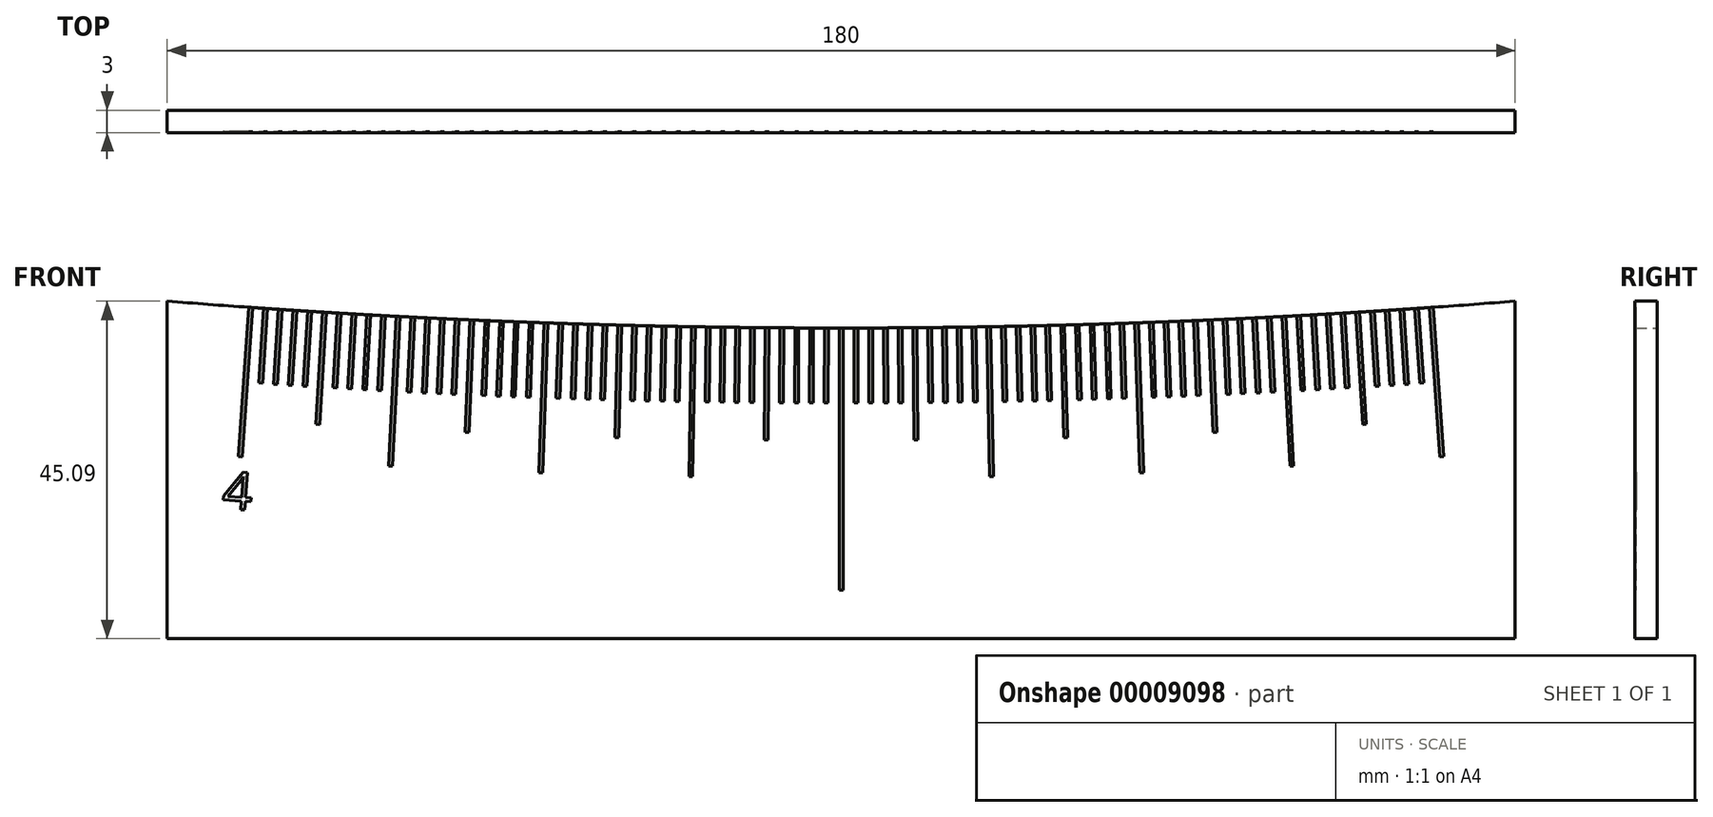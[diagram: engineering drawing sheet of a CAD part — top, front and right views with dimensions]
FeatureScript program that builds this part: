
annotation { "Feature Type Name" : "Feature", "Feature Type Description" : "" }
export const myFeature = defineFeature(function(context is Context, id is Id, definition is map)
    precondition{}
    {
        {
            var Q0;
            Q0=qCreatedBy(makeId("Front.planeOp"),FACE);
            var sketch = newSketch(context, id + "F0", { "sketchPlane" : qUnion([Q0])});
            skCircle(sketch, "E0", {"center": v(0, 1130) * mm, "radius": 1130 * mm});
            skLineSegment(sketch, "E1.rect.bottom", {"start": v(90, -41.5) * mm, "end": v(-90, -41.5) * mm});
            skLineSegment(sketch, "E1.rect.top", {"start": v(90, 41.5) * mm, "end": v(-90, 41.5) * mm});
            skLineSegment(sketch, "E1.rect.left", {"start": v(90, -41.5) * mm, "end": v(90, 41.5) * mm});
            skLineSegment(sketch, "E1.rect.right", {"start": v(-90, -41.5) * mm, "end": v(-90, 41.5) * mm});
            skPoint(sketch, "E1.rect.middle", {"position": v(0, 0) * mm});
            skSolve(sketch);
        }
        {
            var Q0;
            {var subQ3=sQuery(id+"F0.wireOp",EDGE,"E1.rect.bottom");Q0=makeQuery(id+"F0.imprint","IMPRINT",FACE,{"disambiguationData":[TD([[makeQuery(id+"F0.imprint","IMPRINT",EDGE,{"derivedFrom":subQ3}),-1.0]])]});}
            extrude(context, id + "F1", {"entities" : qUnion([Q0]), "depth" : 3 * mm});
        }
        {
            var Q0;
            Q0=makeQuery(id+"F1.opExtrude","CAP_FACE",FACE,{"disambiguationData":[OSD([sQuery(id+"F0.wireOp",EDGE,"E0"),sQuery(id+"F0.wireOp",EDGE,"E1.rect.bottom"),sQuery(id+"F0.wireOp",EDGE,"E1.rect.left"),sQuery(id+"F0.wireOp",EDGE,"E1.rect.right")])],"isStart":false});
            var sketch = newSketch(context, id + "F2", { "sketchPlane" : qUnion([Q0])});
            skLineSegment(sketch, "E2.rect.bottom", {"start": v(0.25, 20) * mm, "end": v(-0.25, 20) * mm});
            skLineSegment(sketch, "E2.rect.top", {"start": v(0.25, -20) * mm, "end": v(-0.25, -20) * mm});
            skLineSegment(sketch, "E2.rect.left", {"start": v(0.25, 20) * mm, "end": v(0.25, -20) * mm});
            skLineSegment(sketch, "E2.rect.right", {"start": v(-0.25, 20) * mm, "end": v(-0.25, -20) * mm});
            skPoint(sketch, "E2.rect.middle", {"position": v(0, 0) * mm});
            skLineSegment(sketch, "E3.1.0", {"start": v(-19.12, 20.16) * mm, "end": v(-19.62, 20.17) * mm});
            skLineSegment(sketch, "E3.1.1", {"start": v(-19.62, 20.17) * mm, "end": v(-20.32, -19.82) * mm});
            skLineSegment(sketch, "E3.1.2", {"start": v(-19.12, 20.16) * mm, "end": v(-19.82, -19.83) * mm});
            skLineSegment(sketch, "E3.1.3", {"start": v(-19.82, -19.83) * mm, "end": v(-20.32, -19.82) * mm});
            skLineSegment(sketch, "E3.2.0", {"start": v(-38.49, 20.67) * mm, "end": v(-38.99, 20.68) * mm});
            skLineSegment(sketch, "E3.2.1", {"start": v(-38.99, 20.68) * mm, "end": v(-40.38, -19.3) * mm});
            skLineSegment(sketch, "E3.2.2", {"start": v(-38.49, 20.67) * mm, "end": v(-39.88, -19.3) * mm});
            skLineSegment(sketch, "E3.2.3", {"start": v(-39.88, -19.3) * mm, "end": v(-40.38, -19.3) * mm});
            skLineSegment(sketch, "E3.3.0", {"start": v(-57.84, 21.5) * mm, "end": v(-58.34, 21.53) * mm});
            skLineSegment(sketch, "E3.3.1", {"start": v(-58.34, 21.53) * mm, "end": v(-60.44, -18.41) * mm});
            skLineSegment(sketch, "E3.3.2", {"start": v(-57.84, 21.5) * mm, "end": v(-59.94, -18.44) * mm});
            skLineSegment(sketch, "E3.3.3", {"start": v(-59.94, -18.44) * mm, "end": v(-60.44, -18.41) * mm});
            skLineSegment(sketch, "E3.4.0", {"start": v(-77.18, 22.69) * mm, "end": v(-77.68, 22.72) * mm});
            skLineSegment(sketch, "E3.4.1", {"start": v(-77.68, 22.72) * mm, "end": v(-80.47, -17.18) * mm});
            skLineSegment(sketch, "E3.4.2", {"start": v(-77.18, 22.69) * mm, "end": v(-79.97, -17.22) * mm});
            skLineSegment(sketch, "E3.4.3", {"start": v(-79.97, -17.22) * mm, "end": v(-80.47, -17.18) * mm});
            skPoint(sketch, "E3.center", {"position": v(0, 1130) * mm});
            skLineSegment(sketch, "E3.anchor1", {"start": v(0, 1130) * mm, "end": v(-0.25, 20) * mm, "construction": true});
            skLineSegment(sketch, "E3.anchor2", {"start": v(0, 1130) * mm, "end": v(-77.68, 22.72) * mm, "construction": true});
            skSolve(sketch);
        }
        {
            var Q0;
            Q0 = qSketchRegion(id + "F2", true);
            extrude(context, id + "F3", {"entities" : qUnion([Q0]), "operationType" : NewBodyOperationType.REMOVE, "oppositeDirection" : true, "depth" : 0.1 * mm});
        }
        {
            var Q0;
            Q0=makeQuery(id+"F1.opExtrude","SWEPT_BODY",BODY,{"disambiguationData":[OSD([sQuery(id+"F0.wireOp",EDGE,"E0"),sQuery(id+"F0.wireOp",EDGE,"E1.rect.bottom"),sQuery(id+"F0.wireOp",EDGE,"E1.rect.left"),sQuery(id+"F0.wireOp",EDGE,"E1.rect.right")])]});
            var Q1;
            Q1=qCreatedBy(makeId("Right.planeOp"),FACE);
            mirror(context, id + "F4", {"operationType" : NewBodyOperationType.INTERSECT, "entities" : qUnion([Q0]), "mirrorPlane" : qUnion([Q1])});
        }
        {
            var Q0;
            Q0=makeQuery(id+"F1.opExtrude","CAP_FACE",FACE,{"disambiguationData":[OSD([sQuery(id+"F0.wireOp",EDGE,"E0"),sQuery(id+"F0.wireOp",EDGE,"E1.rect.bottom"),sQuery(id+"F0.wireOp",EDGE,"E1.rect.left"),sQuery(id+"F0.wireOp",EDGE,"E1.rect.right")])],"isStart":false});
            var sketch = newSketch(context, id + "F5", { "sketchPlane" : qUnion([Q0])});
            skLineSegment(sketch, "E4.rect.bottom", {"start": v(0.25, 10) * mm, "end": v(-0.25, 10) * mm});
            skLineSegment(sketch, "E4.rect.top", {"start": v(0.25, -10) * mm, "end": v(-0.25, -10) * mm});
            skLineSegment(sketch, "E4.rect.left", {"start": v(0.25, 10) * mm, "end": v(0.25, -10) * mm});
            skLineSegment(sketch, "E4.rect.right", {"start": v(-0.25, 10) * mm, "end": v(-0.25, -10) * mm});
            skPoint(sketch, "E4.rect.middle", {"position": v(0, 0) * mm});
            skLineSegment(sketch, "E5.1.0", {"start": v(-1.74, -10) * mm, "end": v(-2.24, -10) * mm});
            skLineSegment(sketch, "E5.1.1", {"start": v(-1.7, 10) * mm, "end": v(-1.74, -10) * mm});
            skLineSegment(sketch, "E5.1.2", {"start": v(-2.2, 10) * mm, "end": v(-2.24, -10) * mm});
            skLineSegment(sketch, "E5.1.3", {"start": v(-1.7, 10) * mm, "end": v(-2.2, 10) * mm});
            skLineSegment(sketch, "E5.2.0", {"start": v(-3.73, -10) * mm, "end": v(-4.23, -10) * mm});
            skLineSegment(sketch, "E5.2.1", {"start": v(-3.66, 10) * mm, "end": v(-3.73, -10) * mm});
            skLineSegment(sketch, "E5.2.2", {"start": v(-4.16, 10) * mm, "end": v(-4.23, -10) * mm});
            skLineSegment(sketch, "E5.2.3", {"start": v(-3.66, 10) * mm, "end": v(-4.16, 10) * mm});
            skLineSegment(sketch, "E5.3.0", {"start": v(-5.72, -9.99) * mm, "end": v(-6.22, -9.98) * mm});
            skLineSegment(sketch, "E5.3.1", {"start": v(-5.61, 10.01) * mm, "end": v(-5.72, -9.99) * mm});
            skLineSegment(sketch, "E5.3.2", {"start": v(-6.11, 10.02) * mm, "end": v(-6.22, -9.98) * mm});
            skLineSegment(sketch, "E5.3.3", {"start": v(-5.61, 10.01) * mm, "end": v(-6.11, 10.02) * mm});
            skLineSegment(sketch, "E5.4.0", {"start": v(-7.7, -9.97) * mm, "end": v(-8.2, -9.97) * mm});
            skLineSegment(sketch, "E5.4.1", {"start": v(-7.57, 10.03) * mm, "end": v(-7.7, -9.97) * mm});
            skLineSegment(sketch, "E5.4.2", {"start": v(-8.07, 10.03) * mm, "end": v(-8.2, -9.97) * mm});
            skLineSegment(sketch, "E5.4.3", {"start": v(-7.57, 10.03) * mm, "end": v(-8.07, 10.03) * mm});
            skLineSegment(sketch, "E5.5.0", {"start": v(-9.7, -9.96) * mm, "end": v(-10.2, -9.95) * mm});
            skLineSegment(sketch, "E5.5.1", {"start": v(-9.52, 10.04) * mm, "end": v(-9.7, -9.96) * mm});
            skLineSegment(sketch, "E5.5.2", {"start": v(-10.02, 10.04) * mm, "end": v(-10.2, -9.95) * mm});
            skLineSegment(sketch, "E5.5.3", {"start": v(-9.52, 10.04) * mm, "end": v(-10.02, 10.04) * mm});
            skLineSegment(sketch, "E5.6.0", {"start": v(-11.69, -9.94) * mm, "end": v(-12.19, -9.93) * mm});
            skLineSegment(sketch, "E5.6.1", {"start": v(-11.48, 10.06) * mm, "end": v(-11.69, -9.94) * mm});
            skLineSegment(sketch, "E5.6.2", {"start": v(-11.98, 10.06) * mm, "end": v(-12.19, -9.93) * mm});
            skLineSegment(sketch, "E5.6.3", {"start": v(-11.48, 10.06) * mm, "end": v(-11.98, 10.06) * mm});
            skLineSegment(sketch, "E5.7.0", {"start": v(-13.68, -9.92) * mm, "end": v(-14.18, -9.91) * mm});
            skLineSegment(sketch, "E5.7.1", {"start": v(-13.43, 10.08) * mm, "end": v(-13.68, -9.92) * mm});
            skLineSegment(sketch, "E5.7.2", {"start": v(-13.93, 10.09) * mm, "end": v(-14.18, -9.91) * mm});
            skLineSegment(sketch, "E5.7.3", {"start": v(-13.43, 10.08) * mm, "end": v(-13.93, 10.09) * mm});
            skLineSegment(sketch, "E5.8.0", {"start": v(-15.67, -9.9) * mm, "end": v(-16.17, -9.89) * mm});
            skLineSegment(sketch, "E5.8.1", {"start": v(-15.39, 10.1) * mm, "end": v(-15.67, -9.9) * mm});
            skLineSegment(sketch, "E5.8.2", {"start": v(-15.89, 10.11) * mm, "end": v(-16.17, -9.89) * mm});
            skLineSegment(sketch, "E5.8.3", {"start": v(-15.39, 10.1) * mm, "end": v(-15.89, 10.11) * mm});
            skLineSegment(sketch, "E5.9.0", {"start": v(-17.66, -9.86) * mm, "end": v(-18.16, -9.86) * mm});
            skLineSegment(sketch, "E5.9.1", {"start": v(-17.34, 10.13) * mm, "end": v(-17.66, -9.86) * mm});
            skLineSegment(sketch, "E5.9.2", {"start": v(-17.84, 10.14) * mm, "end": v(-18.16, -9.86) * mm});
            skLineSegment(sketch, "E5.9.3", {"start": v(-17.34, 10.13) * mm, "end": v(-17.84, 10.14) * mm});
            skLineSegment(sketch, "E5.10.0", {"start": v(-19.65, -9.83) * mm, "end": v(-20.15, -9.82) * mm});
            skLineSegment(sketch, "E5.10.1", {"start": v(-19.3, 10.17) * mm, "end": v(-19.65, -9.83) * mm});
            skLineSegment(sketch, "E5.10.2", {"start": v(-19.8, 10.17) * mm, "end": v(-20.15, -9.82) * mm});
            skLineSegment(sketch, "E5.10.3", {"start": v(-19.3, 10.17) * mm, "end": v(-19.8, 10.17) * mm});
            skLineSegment(sketch, "E5.11.0", {"start": v(-21.64, -9.8) * mm, "end": v(-22.14, -9.79) * mm});
            skLineSegment(sketch, "E5.11.1", {"start": v(-21.25, 10.2) * mm, "end": v(-21.64, -9.8) * mm});
            skLineSegment(sketch, "E5.11.2", {"start": v(-21.75, 10.21) * mm, "end": v(-22.14, -9.79) * mm});
            skLineSegment(sketch, "E5.11.3", {"start": v(-21.25, 10.2) * mm, "end": v(-21.75, 10.21) * mm});
            skLineSegment(sketch, "E5.12.0", {"start": v(-23.62, -9.76) * mm, "end": v(-24.12, -9.74) * mm});
            skLineSegment(sketch, "E5.12.1", {"start": v(-23.2, 10.24) * mm, "end": v(-23.62, -9.76) * mm});
            skLineSegment(sketch, "E5.12.2", {"start": v(-23.7, 10.25) * mm, "end": v(-24.12, -9.74) * mm});
            skLineSegment(sketch, "E5.12.3", {"start": v(-23.2, 10.24) * mm, "end": v(-23.7, 10.25) * mm});
            skLineSegment(sketch, "E5.13.0", {"start": v(-25.61, -9.71) * mm, "end": v(-26.11, -9.7) * mm});
            skLineSegment(sketch, "E5.13.1", {"start": v(-25.16, 10.28) * mm, "end": v(-25.61, -9.71) * mm});
            skLineSegment(sketch, "E5.13.2", {"start": v(-25.66, 10.3) * mm, "end": v(-26.11, -9.7) * mm});
            skLineSegment(sketch, "E5.13.3", {"start": v(-25.16, 10.28) * mm, "end": v(-25.66, 10.3) * mm});
            skLineSegment(sketch, "E5.14.0", {"start": v(-27.6, -9.67) * mm, "end": v(-28.1, -9.65) * mm});
            skLineSegment(sketch, "E5.14.1", {"start": v(-27.11, 10.33) * mm, "end": v(-27.6, -9.67) * mm});
            skLineSegment(sketch, "E5.14.2", {"start": v(-27.61, 10.34) * mm, "end": v(-28.1, -9.65) * mm});
            skLineSegment(sketch, "E5.14.3", {"start": v(-27.11, 10.33) * mm, "end": v(-27.61, 10.34) * mm});
            skLineSegment(sketch, "E5.15.0", {"start": v(-29.6, -9.62) * mm, "end": v(-30.1, -9.6) * mm});
            skLineSegment(sketch, "E5.15.1", {"start": v(-29.07, 10.38) * mm, "end": v(-29.6, -9.62) * mm});
            skLineSegment(sketch, "E5.15.2", {"start": v(-29.57, 10.4) * mm, "end": v(-30.1, -9.6) * mm});
            skLineSegment(sketch, "E5.15.3", {"start": v(-29.07, 10.38) * mm, "end": v(-29.57, 10.4) * mm});
            skLineSegment(sketch, "E5.16.0", {"start": v(-31.58, -9.56) * mm, "end": v(-32.08, -9.55) * mm});
            skLineSegment(sketch, "E5.16.1", {"start": v(-31.02, 10.43) * mm, "end": v(-31.58, -9.56) * mm});
            skLineSegment(sketch, "E5.16.2", {"start": v(-31.52, 10.44) * mm, "end": v(-32.08, -9.55) * mm});
            skLineSegment(sketch, "E5.16.3", {"start": v(-31.02, 10.43) * mm, "end": v(-31.52, 10.44) * mm});
            skLineSegment(sketch, "E5.17.0", {"start": v(-33.57, -9.5) * mm, "end": v(-34.07, -9.5) * mm});
            skLineSegment(sketch, "E5.17.1", {"start": v(-32.98, 10.49) * mm, "end": v(-33.57, -9.5) * mm});
            skLineSegment(sketch, "E5.17.2", {"start": v(-33.48, 10.5) * mm, "end": v(-34.07, -9.5) * mm});
            skLineSegment(sketch, "E5.17.3", {"start": v(-32.98, 10.49) * mm, "end": v(-33.48, 10.5) * mm});
            skLineSegment(sketch, "E5.18.0", {"start": v(-35.56, -9.45) * mm, "end": v(-36.06, -9.43) * mm});
            skLineSegment(sketch, "E5.18.1", {"start": v(-34.93, 10.54) * mm, "end": v(-35.56, -9.45) * mm});
            skLineSegment(sketch, "E5.18.2", {"start": v(-35.43, 10.56) * mm, "end": v(-36.06, -9.43) * mm});
            skLineSegment(sketch, "E5.18.3", {"start": v(-34.93, 10.54) * mm, "end": v(-35.43, 10.56) * mm});
            skLineSegment(sketch, "E5.19.0", {"start": v(-37.55, -9.38) * mm, "end": v(-38.05, -9.36) * mm});
            skLineSegment(sketch, "E5.19.1", {"start": v(-36.88, 10.6) * mm, "end": v(-37.55, -9.38) * mm});
            skLineSegment(sketch, "E5.19.2", {"start": v(-37.38, 10.62) * mm, "end": v(-38.05, -9.36) * mm});
            skLineSegment(sketch, "E5.19.3", {"start": v(-36.88, 10.6) * mm, "end": v(-37.38, 10.62) * mm});
            skLineSegment(sketch, "E5.20.0", {"start": v(-39.54, -9.31) * mm, "end": v(-40.04, -9.3) * mm});
            skLineSegment(sketch, "E5.20.1", {"start": v(-38.84, 10.67) * mm, "end": v(-39.54, -9.31) * mm});
            skLineSegment(sketch, "E5.20.2", {"start": v(-39.34, 10.7) * mm, "end": v(-40.04, -9.3) * mm});
            skLineSegment(sketch, "E5.20.3", {"start": v(-38.84, 10.67) * mm, "end": v(-39.34, 10.7) * mm});
            skLineSegment(sketch, "E5.21.0", {"start": v(-41.52, -9.24) * mm, "end": v(-42.02, -9.23) * mm});
            skLineSegment(sketch, "E5.21.1", {"start": v(-40.8, 10.74) * mm, "end": v(-41.52, -9.24) * mm});
            skLineSegment(sketch, "E5.21.2", {"start": v(-41.3, 10.76) * mm, "end": v(-42.02, -9.23) * mm});
            skLineSegment(sketch, "E5.21.3", {"start": v(-40.8, 10.74) * mm, "end": v(-41.3, 10.76) * mm});
            skLineSegment(sketch, "E5.22.0", {"start": v(-43.51, -9.17) * mm, "end": v(-44.01, -9.15) * mm});
            skLineSegment(sketch, "E5.22.1", {"start": v(-42.74, 10.82) * mm, "end": v(-43.51, -9.17) * mm});
            skLineSegment(sketch, "E5.22.2", {"start": v(-43.24, 10.84) * mm, "end": v(-44.01, -9.15) * mm});
            skLineSegment(sketch, "E5.22.3", {"start": v(-42.74, 10.82) * mm, "end": v(-43.24, 10.84) * mm});
            skLineSegment(sketch, "E5.23.0", {"start": v(-45.5, -9.1) * mm, "end": v(-46, -9.07) * mm});
            skLineSegment(sketch, "E5.23.1", {"start": v(-44.7, 10.9) * mm, "end": v(-45.5, -9.1) * mm});
            skLineSegment(sketch, "E5.23.2", {"start": v(-45.2, 10.91) * mm, "end": v(-46, -9.07) * mm});
            skLineSegment(sketch, "E5.23.3", {"start": v(-44.7, 10.9) * mm, "end": v(-45.2, 10.91) * mm});
            skLineSegment(sketch, "E5.24.0", {"start": v(-47.49, -9.01) * mm, "end": v(-47.99, -8.99) * mm});
            skLineSegment(sketch, "E5.24.1", {"start": v(-46.65, 10.97) * mm, "end": v(-47.49, -9.01) * mm});
            skLineSegment(sketch, "E5.24.2", {"start": v(-47.15, 11) * mm, "end": v(-47.99, -8.99) * mm});
            skLineSegment(sketch, "E5.24.3", {"start": v(-46.65, 10.97) * mm, "end": v(-47.15, 11) * mm});
            skLineSegment(sketch, "E5.25.0", {"start": v(-49.48, -8.93) * mm, "end": v(-49.98, -8.9) * mm});
            skLineSegment(sketch, "E5.25.1", {"start": v(-48.6, 11.06) * mm, "end": v(-49.48, -8.93) * mm});
            skLineSegment(sketch, "E5.25.2", {"start": v(-49.1, 11.08) * mm, "end": v(-49.98, -8.9) * mm});
            skLineSegment(sketch, "E5.25.3", {"start": v(-48.6, 11.06) * mm, "end": v(-49.1, 11.08) * mm});
            skLineSegment(sketch, "E5.26.0", {"start": v(-51.46, -8.84) * mm, "end": v(-51.96, -8.82) * mm});
            skLineSegment(sketch, "E5.26.1", {"start": v(-50.56, 11.14) * mm, "end": v(-51.46, -8.84) * mm});
            skLineSegment(sketch, "E5.26.2", {"start": v(-51.06, 11.16) * mm, "end": v(-51.96, -8.82) * mm});
            skLineSegment(sketch, "E5.26.3", {"start": v(-50.56, 11.14) * mm, "end": v(-51.06, 11.16) * mm});
            skLineSegment(sketch, "E5.27.0", {"start": v(-53.45, -8.75) * mm, "end": v(-53.95, -8.72) * mm});
            skLineSegment(sketch, "E5.27.1", {"start": v(-52.5, 11.23) * mm, "end": v(-53.45, -8.75) * mm});
            skLineSegment(sketch, "E5.27.2", {"start": v(-53, 11.26) * mm, "end": v(-53.95, -8.72) * mm});
            skLineSegment(sketch, "E5.27.3", {"start": v(-52.5, 11.23) * mm, "end": v(-53, 11.26) * mm});
            skLineSegment(sketch, "E5.28.0", {"start": v(-55.44, -8.65) * mm, "end": v(-55.94, -8.63) * mm});
            skLineSegment(sketch, "E5.28.1", {"start": v(-54.46, 11.32) * mm, "end": v(-55.44, -8.65) * mm});
            skLineSegment(sketch, "E5.28.2", {"start": v(-54.96, 11.35) * mm, "end": v(-55.94, -8.63) * mm});
            skLineSegment(sketch, "E5.28.3", {"start": v(-54.46, 11.32) * mm, "end": v(-54.96, 11.35) * mm});
            skLineSegment(sketch, "E5.29.0", {"start": v(-57.43, -8.55) * mm, "end": v(-57.93, -8.53) * mm});
            skLineSegment(sketch, "E5.29.1", {"start": v(-56.41, 11.42) * mm, "end": v(-57.43, -8.55) * mm});
            skLineSegment(sketch, "E5.29.2", {"start": v(-56.91, 11.45) * mm, "end": v(-57.93, -8.53) * mm});
            skLineSegment(sketch, "E5.29.3", {"start": v(-56.41, 11.42) * mm, "end": v(-56.91, 11.45) * mm});
            skLineSegment(sketch, "E5.30.0", {"start": v(-59.41, -8.45) * mm, "end": v(-59.91, -8.42) * mm});
            skLineSegment(sketch, "E5.30.1", {"start": v(-58.37, 11.52) * mm, "end": v(-59.41, -8.45) * mm});
            skLineSegment(sketch, "E5.30.2", {"start": v(-58.87, 11.55) * mm, "end": v(-59.91, -8.42) * mm});
            skLineSegment(sketch, "E5.30.3", {"start": v(-58.37, 11.52) * mm, "end": v(-58.87, 11.55) * mm});
            skLineSegment(sketch, "E5.31.0", {"start": v(-61.4, -8.35) * mm, "end": v(-61.9, -8.32) * mm});
            skLineSegment(sketch, "E5.31.1", {"start": v(-60.32, 11.63) * mm, "end": v(-61.4, -8.35) * mm});
            skLineSegment(sketch, "E5.31.2", {"start": v(-60.82, 11.65) * mm, "end": v(-61.9, -8.32) * mm});
            skLineSegment(sketch, "E5.31.3", {"start": v(-60.32, 11.63) * mm, "end": v(-60.82, 11.65) * mm});
            skLineSegment(sketch, "E5.32.0", {"start": v(-63.39, -8.24) * mm, "end": v(-63.89, -8.2) * mm});
            skLineSegment(sketch, "E5.32.1", {"start": v(-62.27, 11.73) * mm, "end": v(-63.39, -8.24) * mm});
            skLineSegment(sketch, "E5.32.2", {"start": v(-62.77, 11.76) * mm, "end": v(-63.89, -8.2) * mm});
            skLineSegment(sketch, "E5.32.3", {"start": v(-62.27, 11.73) * mm, "end": v(-62.77, 11.76) * mm});
            skLineSegment(sketch, "E5.33.0", {"start": v(-65.37, -8.12) * mm, "end": v(-65.87, -8.1) * mm});
            skLineSegment(sketch, "E5.33.1", {"start": v(-64.22, 11.84) * mm, "end": v(-65.37, -8.12) * mm});
            skLineSegment(sketch, "E5.33.2", {"start": v(-64.72, 11.87) * mm, "end": v(-65.87, -8.1) * mm});
            skLineSegment(sketch, "E5.33.3", {"start": v(-64.22, 11.84) * mm, "end": v(-64.72, 11.87) * mm});
            skLineSegment(sketch, "E5.34.0", {"start": v(-67.36, -8) * mm, "end": v(-67.86, -7.98) * mm});
            skLineSegment(sketch, "E5.34.1", {"start": v(-66.17, 11.96) * mm, "end": v(-67.36, -8) * mm});
            skLineSegment(sketch, "E5.34.2", {"start": v(-66.67, 11.99) * mm, "end": v(-67.86, -7.98) * mm});
            skLineSegment(sketch, "E5.34.3", {"start": v(-66.17, 11.96) * mm, "end": v(-66.67, 11.99) * mm});
            skLineSegment(sketch, "E5.35.0", {"start": v(-69.35, -7.89) * mm, "end": v(-69.84, -7.86) * mm});
            skLineSegment(sketch, "E5.35.1", {"start": v(-68.12, 12.07) * mm, "end": v(-69.35, -7.89) * mm});
            skLineSegment(sketch, "E5.35.2", {"start": v(-68.62, 12.1) * mm, "end": v(-69.84, -7.86) * mm});
            skLineSegment(sketch, "E5.35.3", {"start": v(-68.12, 12.07) * mm, "end": v(-68.62, 12.1) * mm});
            skLineSegment(sketch, "E5.36.0", {"start": v(-71.33, -7.77) * mm, "end": v(-71.83, -7.73) * mm});
            skLineSegment(sketch, "E5.36.1", {"start": v(-70.08, 12.2) * mm, "end": v(-71.33, -7.77) * mm});
            skLineSegment(sketch, "E5.36.2", {"start": v(-70.57, 12.23) * mm, "end": v(-71.83, -7.73) * mm});
            skLineSegment(sketch, "E5.36.3", {"start": v(-70.08, 12.2) * mm, "end": v(-70.57, 12.23) * mm});
            skLineSegment(sketch, "E5.37.0", {"start": v(-73.32, -7.64) * mm, "end": v(-73.82, -7.6) * mm});
            skLineSegment(sketch, "E5.37.1", {"start": v(-72.03, 12.32) * mm, "end": v(-73.32, -7.64) * mm});
            skLineSegment(sketch, "E5.37.2", {"start": v(-72.53, 12.35) * mm, "end": v(-73.82, -7.6) * mm});
            skLineSegment(sketch, "E5.37.3", {"start": v(-72.03, 12.32) * mm, "end": v(-72.53, 12.35) * mm});
            skLineSegment(sketch, "E5.38.0", {"start": v(-75.3, -7.51) * mm, "end": v(-75.8, -7.48) * mm});
            skLineSegment(sketch, "E5.38.1", {"start": v(-73.98, 12.45) * mm, "end": v(-75.3, -7.51) * mm});
            skLineSegment(sketch, "E5.38.2", {"start": v(-74.48, 12.48) * mm, "end": v(-75.8, -7.48) * mm});
            skLineSegment(sketch, "E5.38.3", {"start": v(-73.98, 12.45) * mm, "end": v(-74.48, 12.48) * mm});
            skLineSegment(sketch, "E5.39.0", {"start": v(-77.29, -7.38) * mm, "end": v(-77.79, -7.34) * mm});
            skLineSegment(sketch, "E5.39.1", {"start": v(-75.93, 12.58) * mm, "end": v(-77.29, -7.38) * mm});
            skLineSegment(sketch, "E5.39.2", {"start": v(-76.43, 12.61) * mm, "end": v(-77.79, -7.34) * mm});
            skLineSegment(sketch, "E5.39.3", {"start": v(-75.93, 12.58) * mm, "end": v(-76.43, 12.61) * mm});
            skPoint(sketch, "E5.center", {"position": v(0, 1130) * mm});
            skLineSegment(sketch, "E5.anchor1", {"start": v(0, 1130) * mm, "end": v(-0.25, -10) * mm, "construction": true});
            skLineSegment(sketch, "E5.anchor2", {"start": v(0, 1130) * mm, "end": v(-79.77, -7.2) * mm, "construction": true});
            skLineSegment(sketch, "E6.2.40.0", {"start": v(-79.27, -7.24) * mm, "end": v(-79.77, -7.2) * mm});
            skLineSegment(sketch, "E6.3.40.0", {"start": v(-77.88, 12.71) * mm, "end": v(-79.27, -7.24) * mm});
            skLineSegment(sketch, "E6.6.40.0", {"start": v(-78.38, 12.75) * mm, "end": v(-79.77, -7.2) * mm});
            skLineSegment(sketch, "E6.9.40.0", {"start": v(-77.88, 12.71) * mm, "end": v(-78.38, 12.75) * mm});
            skSolve(sketch);
        }
        {
            var Q0;
            Q0 = qSketchRegion(id + "F5", true);
            extrude(context, id + "F6", {"entities" : qUnion([Q0]), "operationType" : NewBodyOperationType.REMOVE, "oppositeDirection" : true, "depth" : 0.1 * mm});
        }
        {
            var Q0;
            Q0=makeQuery(id+"F1.opExtrude","SWEPT_BODY",BODY,{"disambiguationData":[OSD([sQuery(id+"F0.wireOp",EDGE,"E0"),sQuery(id+"F0.wireOp",EDGE,"E1.rect.bottom"),sQuery(id+"F0.wireOp",EDGE,"E1.rect.left"),sQuery(id+"F0.wireOp",EDGE,"E1.rect.right")])]});
            var Q1;
            Q1=qCreatedBy(makeId("Right.planeOp"),FACE);
            mirror(context, id + "F7", {"operationType" : NewBodyOperationType.INTERSECT, "entities" : qUnion([Q0]), "mirrorPlane" : qUnion([Q1])});
        }
        {
            var Q0;
            Q0=makeQuery(id+"F1.opExtrude","CAP_FACE",FACE,{"disambiguationData":[OSD([sQuery(id+"F0.wireOp",EDGE,"E0"),sQuery(id+"F0.wireOp",EDGE,"E1.rect.bottom"),sQuery(id+"F0.wireOp",EDGE,"E1.rect.left"),sQuery(id+"F0.wireOp",EDGE,"E1.rect.right")])],"isStart":false});
            var sketch = newSketch(context, id + "F8", { "sketchPlane" : qUnion([Q0])});
            skLineSegment(sketch, "E7.rect.bottom", {"start": v(-0.25, -35) * mm, "end": v(0.25, -35) * mm});
            skLineSegment(sketch, "E7.rect.top", {"start": v(-0.25, 35) * mm, "end": v(0.25, 35) * mm});
            skLineSegment(sketch, "E7.rect.left", {"start": v(-0.25, -35) * mm, "end": v(-0.25, 35) * mm});
            skLineSegment(sketch, "E7.rect.right", {"start": v(0.25, -35) * mm, "end": v(0.25, 35) * mm});
            skPoint(sketch, "E7.rect.middle", {"position": v(0, 0) * mm});
            skSolve(sketch);
        }
        {
            var Q0;
            Q0 = qSketchRegion(id + "F8", true);
            extrude(context, id + "F9", {"entities" : qUnion([Q0]), "operationType" : NewBodyOperationType.REMOVE, "oppositeDirection" : true, "depth" : 0.1 * mm});
        }
        {
            var Q0;
            Q0=makeQuery(id+"F1.opExtrude","CAP_FACE",FACE,{"disambiguationData":[OSD([sQuery(id+"F0.wireOp",EDGE,"E0"),sQuery(id+"F0.wireOp",EDGE,"E1.rect.bottom"),sQuery(id+"F0.wireOp",EDGE,"E1.rect.left"),sQuery(id+"F0.wireOp",EDGE,"E1.rect.right")])],"isStart":false});
            var sketch = newSketch(context, id + "F10", { "sketchPlane" : qUnion([Q0])});
            skLineSegment(sketch, "E8.rect.bottom", {"start": v(-0.25, -15) * mm, "end": v(0.25, -15) * mm});
            skLineSegment(sketch, "E8.rect.top", {"start": v(-0.25, 15) * mm, "end": v(0.25, 15) * mm});
            skLineSegment(sketch, "E8.rect.left", {"start": v(-0.25, -15) * mm, "end": v(-0.25, 15) * mm});
            skLineSegment(sketch, "E8.rect.right", {"start": v(0.25, -15) * mm, "end": v(0.25, 15) * mm});
            skPoint(sketch, "E8.rect.middle", {"position": v(0, 0) * mm});
            skLineSegment(sketch, "E9.1.0", {"start": v(-10.24, -14.95) * mm, "end": v(-9.74, -14.96) * mm});
            skLineSegment(sketch, "E9.1.1", {"start": v(-9.74, -14.96) * mm, "end": v(-9.48, 15.04) * mm});
            skLineSegment(sketch, "E9.1.2", {"start": v(-10.24, -14.95) * mm, "end": v(-9.98, 15.04) * mm});
            skLineSegment(sketch, "E9.1.3", {"start": v(-9.98, 15.04) * mm, "end": v(-9.48, 15.04) * mm});
            skLineSegment(sketch, "E9.2.0", {"start": v(-20.23, -14.82) * mm, "end": v(-19.73, -14.83) * mm});
            skLineSegment(sketch, "E9.2.1", {"start": v(-19.73, -14.83) * mm, "end": v(-19.2, 15.17) * mm});
            skLineSegment(sketch, "E9.2.2", {"start": v(-20.23, -14.82) * mm, "end": v(-19.7, 15.17) * mm});
            skLineSegment(sketch, "E9.2.3", {"start": v(-19.7, 15.17) * mm, "end": v(-19.2, 15.17) * mm});
            skLineSegment(sketch, "E9.3.0", {"start": v(-30.22, -14.6) * mm, "end": v(-29.72, -14.61) * mm});
            skLineSegment(sketch, "E9.3.1", {"start": v(-29.72, -14.61) * mm, "end": v(-28.94, 15.38) * mm});
            skLineSegment(sketch, "E9.3.2", {"start": v(-30.22, -14.6) * mm, "end": v(-29.44, 15.39) * mm});
            skLineSegment(sketch, "E9.3.3", {"start": v(-29.44, 15.39) * mm, "end": v(-28.94, 15.38) * mm});
            skLineSegment(sketch, "E9.4.0", {"start": v(-40.2, -14.3) * mm, "end": v(-39.71, -14.31) * mm});
            skLineSegment(sketch, "E9.4.1", {"start": v(-39.71, -14.31) * mm, "end": v(-38.66, 15.67) * mm});
            skLineSegment(sketch, "E9.4.2", {"start": v(-40.2, -14.3) * mm, "end": v(-39.16, 15.69) * mm});
            skLineSegment(sketch, "E9.4.3", {"start": v(-39.16, 15.69) * mm, "end": v(-38.66, 15.67) * mm});
            skLineSegment(sketch, "E9.5.0", {"start": v(-50.2, -13.9) * mm, "end": v(-49.7, -13.92) * mm});
            skLineSegment(sketch, "E9.5.1", {"start": v(-49.7, -13.92) * mm, "end": v(-48.39, 16.05) * mm});
            skLineSegment(sketch, "E9.5.2", {"start": v(-50.2, -13.9) * mm, "end": v(-48.89, 16.07) * mm});
            skLineSegment(sketch, "E9.5.3", {"start": v(-48.89, 16.07) * mm, "end": v(-48.39, 16.05) * mm});
            skLineSegment(sketch, "E9.6.0", {"start": v(-60.17, -13.42) * mm, "end": v(-59.68, -13.44) * mm});
            skLineSegment(sketch, "E9.6.1", {"start": v(-59.68, -13.44) * mm, "end": v(-58.1, 16.51) * mm});
            skLineSegment(sketch, "E9.6.2", {"start": v(-60.17, -13.42) * mm, "end": v(-58.6, 16.54) * mm});
            skLineSegment(sketch, "E9.6.3", {"start": v(-58.6, 16.54) * mm, "end": v(-58.1, 16.51) * mm});
            skLineSegment(sketch, "E9.7.0", {"start": v(-70.15, -12.85) * mm, "end": v(-69.65, -12.88) * mm});
            skLineSegment(sketch, "E9.7.1", {"start": v(-69.65, -12.88) * mm, "end": v(-67.82, 17.06) * mm});
            skLineSegment(sketch, "E9.7.2", {"start": v(-70.15, -12.85) * mm, "end": v(-68.32, 17.1) * mm});
            skLineSegment(sketch, "E9.7.3", {"start": v(-68.32, 17.1) * mm, "end": v(-67.82, 17.06) * mm});
            skLineSegment(sketch, "E9.8.0", {"start": v(-80.12, -12.2) * mm, "end": v(-79.62, -12.23) * mm});
            skLineSegment(sketch, "E9.8.1", {"start": v(-79.62, -12.23) * mm, "end": v(-77.53, 17.7) * mm});
            skLineSegment(sketch, "E9.8.2", {"start": v(-80.12, -12.2) * mm, "end": v(-78.03, 17.73) * mm});
            skLineSegment(sketch, "E9.8.3", {"start": v(-78.03, 17.73) * mm, "end": v(-77.53, 17.7) * mm});
            skPoint(sketch, "E9.center", {"position": v(0, 1130) * mm});
            skLineSegment(sketch, "E9.anchor1", {"start": v(0, 1130) * mm, "end": v(-0.25, -15) * mm, "construction": true});
            skLineSegment(sketch, "E9.anchor2", {"start": v(0, 1130) * mm, "end": v(-80.12, -12.2) * mm, "construction": true});
            skSolve(sketch);
        }
        {
            var Q0;
            Q0 = qSketchRegion(id + "F10", true);
            extrude(context, id + "F11", {"entities" : qUnion([Q0]), "operationType" : NewBodyOperationType.REMOVE, "oppositeDirection" : true, "depth" : 0.1 * mm});
        }
        {
            var Q0;
            Q0=makeQuery(id+"F1.opExtrude","SWEPT_BODY",BODY,{"disambiguationData":[OSD([sQuery(id+"F0.wireOp",EDGE,"E0"),sQuery(id+"F0.wireOp",EDGE,"E1.rect.bottom"),sQuery(id+"F0.wireOp",EDGE,"E1.rect.left"),sQuery(id+"F0.wireOp",EDGE,"E1.rect.right")])]});
            var Q1;
            Q1=qCreatedBy(makeId("Right.planeOp"),FACE);
            mirror(context, id + "F12", {"operationType" : NewBodyOperationType.INTERSECT, "entities" : qUnion([Q0]), "mirrorPlane" : qUnion([Q1])});
        }
        {
            var Q0;
            Q0=makeQuery(id+"F1.opExtrude","CAP_FACE",FACE,{"disambiguationData":[OSD([sQuery(id+"F0.wireOp",EDGE,"E0"),sQuery(id+"F0.wireOp",EDGE,"E1.rect.bottom"),sQuery(id+"F0.wireOp",EDGE,"E1.rect.left"),sQuery(id+"F0.wireOp",EDGE,"E1.rect.right")])],"isStart":false});
            var sketch = newSketch(context, id + "F13", { "sketchPlane" : qUnion([Q0])});
            skText(sketch, "E10", { "text": "4\n", "fontName": "OpenSans-Regular.ttf"});
            const initialGuessF13  = {"E10": [-0.08273, -0.02406, 0.99756, -0.06976, 0.005]};
            skSetInitialGuess(sketch, initialGuessF13);
            skSolve(sketch);
        }
        {
            var Q0;
            Q0 = qSketchRegion(id + "F13", true);
            extrude(context, id + "F14", {"entities" : qUnion([Q0]), "operationType" : NewBodyOperationType.REMOVE, "oppositeDirection" : true, "depth" : 0.2 * mm});
        }
    });
